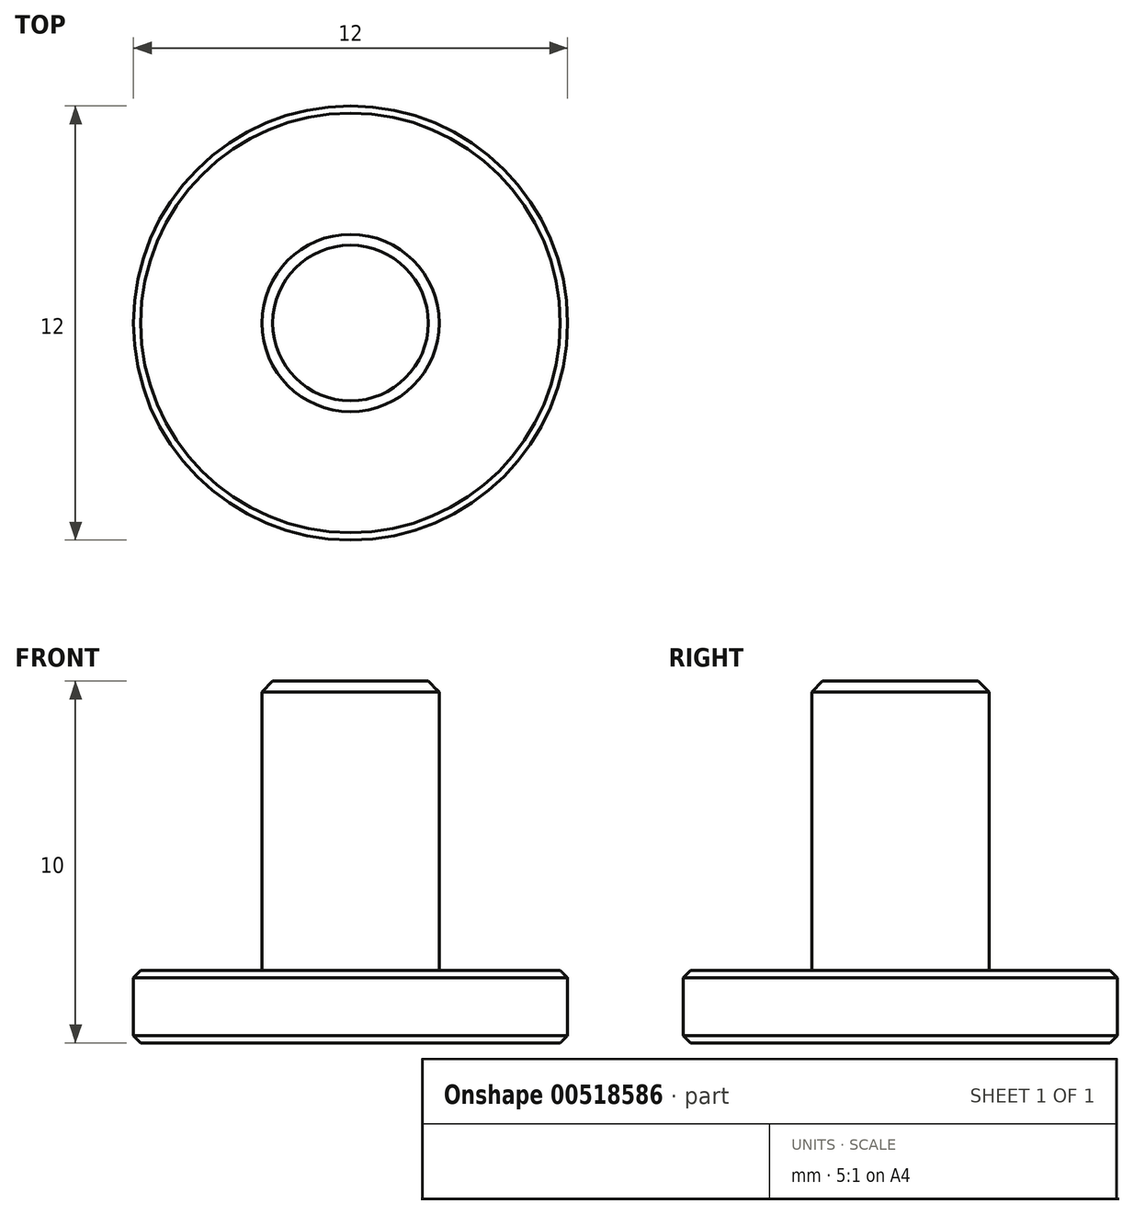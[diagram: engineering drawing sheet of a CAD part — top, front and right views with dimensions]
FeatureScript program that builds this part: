
annotation { "Feature Type Name" : "Feature", "Feature Type Description" : "" }
export const myFeature = defineFeature(function(context is Context, id is Id, definition is map)
    precondition{}
    {
        {
            var Q0;
            Q0=qCreatedBy(makeId("Top.planeOp"),FACE);
            var sketch = newSketch(context, id + "F0", { "sketchPlane" : qUnion([Q0])});
            skCircle(sketch, "E0", {"center": v(0, 0) * mm, "radius": 6 * mm});
            skSolve(sketch);
        }
        {
            var Q0;
            Q0 = qSketchRegion(id + "F0", true);
            extrude(context, id + "F1", {"entities" : qUnion([Q0]), "depth" : 2 * mm, "offsetDistance" : 25 * mm});
        }
        {
            var Q0;
            Q0=makeQuery(id+"F1.opExtrude","CAP_FACE",FACE,{"disambiguationData":[OSD([sQuery(id+"F0.wireOp",EDGE,"E0")])],"isStart":false});
            var sketch = newSketch(context, id + "F2", { "sketchPlane" : qUnion([Q0])});
            skCircle(sketch, "E1", {"center": v(0, 0) * mm, "radius": 2.45 * mm});
            skSolve(sketch);
        }
        {
            var Q0;
            Q0=makeQuery(id+"F2.imprint","IMPRINT",FACE,{"disambiguationData":[TD([[makeQuery(id+"F2.imprint","IMPRINT",EDGE,{"derivedFrom":sQuery(id+"F2.wireOp",EDGE,"E1")}),1.0]])]});
            extrude(context, id + "F3", {"entities" : qUnion([Q0]), "operationType" : NewBodyOperationType.ADD, "depth" : 8 * mm, "offsetDistance" : 25 * mm});
        }
        {
            var Q0;
            Q0=makeQuery(id+"F3.opExtrude","CAP_EDGE",EDGE,{"disambiguationData":[OSD([sQuery(id+"F2.wireOp",EDGE,"E1")])],"isStart":false});
            chamfer(context, id + "F4", {"entities" : qUnion([Q0]), "width" : 0.3 * mm, "tangentPropagation" : true});
        }
        {
            var Q0;
            Q0=makeQuery(id+"F1.opExtrude","CAP_EDGE",EDGE,{"disambiguationData":[OSD([sQuery(id+"F0.wireOp",EDGE,"E0")])],"isStart":false});
            var Q1;
            Q1=makeQuery(id+"F1.opExtrude","CAP_EDGE",EDGE,{"disambiguationData":[OSD([sQuery(id+"F0.wireOp",EDGE,"E0")])],"isStart":true});
            chamfer(context, id + "F5", {"entities" : qUnion([Q0, Q1]), "width" : 0.2 * mm, "tangentPropagation" : true});
        }
    });
